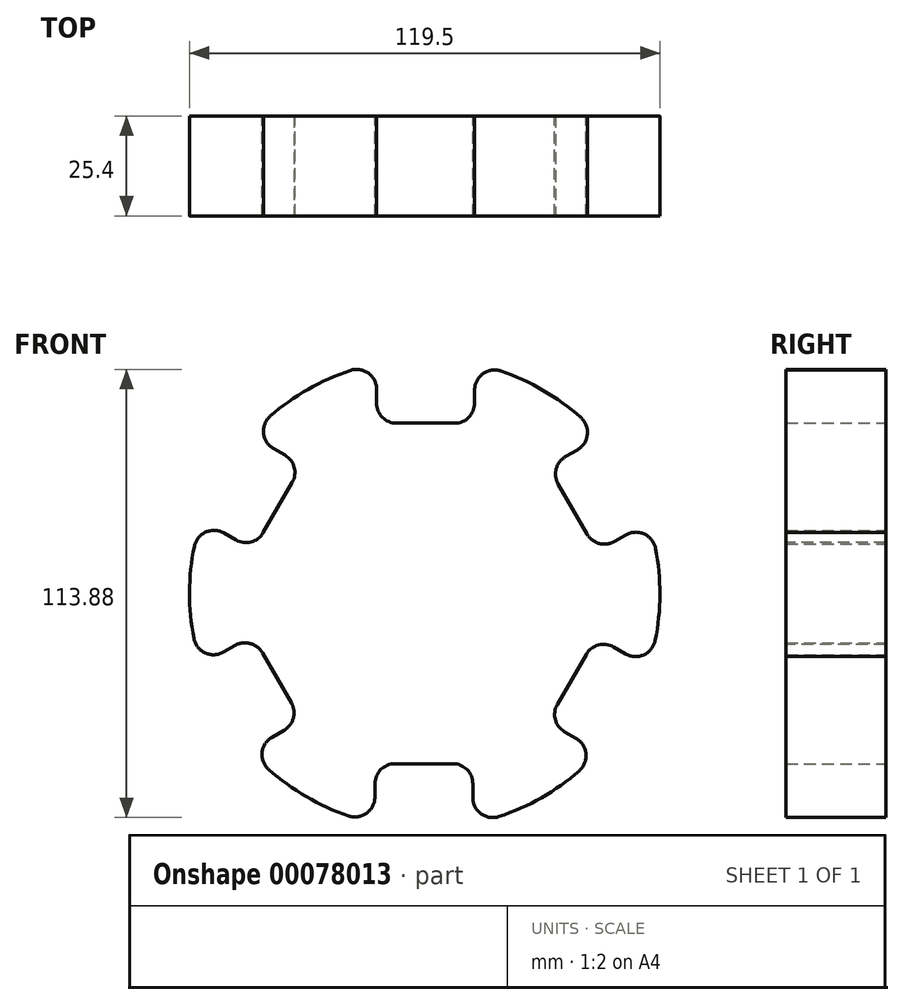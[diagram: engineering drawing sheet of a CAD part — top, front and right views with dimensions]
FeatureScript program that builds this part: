
annotation { "Feature Type Name" : "Feature", "Feature Type Description" : "" }
export const myFeature = defineFeature(function(context is Context, id is Id, definition is map)
    precondition{}
    {
        {
            var Q0;
            Q0=qCreatedBy(makeId("Front.planeOp"),FACE);
            var sketch = newSketch(context, id + "F0", { "sketchPlane" : qUnion([Q0])});
            skCircle(sketch, "E0", {"center": v(0, 0) * mm, "radius": 59.75 * mm});
            skSolve(sketch);
        }
        {
            var Q0;
            Q0=makeQuery(id+"F0.imprint","IMPRINT",FACE,{"disambiguationData":[TD([[makeQuery(id+"F0.imprint","IMPRINT",EDGE,{"derivedFrom":sQuery(id+"F0.wireOp",EDGE,"E0")}),1.0]])]});
            extrude(context, id + "F1", {"entities" : qUnion([Q0]), "depth" : 25.4 * mm});
        }
        {
            var Q0;
            Q0=qCreatedBy(makeId("Top.planeOp"),FACE);
            var sketch = newSketch(context, id + "F5", { "sketchPlane" : qUnion([Q0])});
            skLineSegment(sketch, "E1", {"start": v(0, 57.44) * mm, "end": v(0, -61.35) * mm, "construction": true});
            skSolve(sketch);
        }
        {
            var Q0;
            Q0=qCreatedBy(makeId("Front.planeOp"),FACE);
            var sketch = newSketch(context, id + "F2", { "sketchPlane" : qUnion([Q0])});
            skLineSegment(sketch, "E2.bottom", {"start": v(-12.22, 105.83) * mm, "end": v(12.67, 105.83) * mm});
            skLineSegment(sketch, "E2.top", {"start": v(-12.22, 43.26) * mm, "end": v(12.67, 43.26) * mm});
            skLineSegment(sketch, "E2.left", {"start": v(-12.22, 105.83) * mm, "end": v(-12.22, 43.26) * mm});
            skLineSegment(sketch, "E2.right", {"start": v(12.67, 105.83) * mm, "end": v(12.67, 43.26) * mm});
            skSolve(sketch);
        }
        {
            var Q0;
            Q0=makeQuery(id+"F2.imprint","IMPRINT",FACE,{"disambiguationData":[TD([[makeQuery(id+"F2.imprint","IMPRINT",EDGE,{"derivedFrom":sQuery(id+"F2.wireOp",EDGE,"E2.bottom")}),-1.0]])]});
            extrude(context, id + "F6", {"entities" : qUnion([Q0]), "operationType" : NewBodyOperationType.REMOVE, "depth" : 25.4 * mm});
        }
        {
            var Q0;
            Q0=makeQuery(id+"F6.boolean.opBoolean","INTERSECT",EDGE,{"derivedFrom":[makeQuery(id+"F1.opExtrude","SWEPT_FACE",FACE,{"disambiguationData":[OSD([sQuery(id+"F0.wireOp",EDGE,"E0")])]}),makeQuery(id+"F6.opExtrude","SWEPT_FACE",FACE,{"disambiguationData":[OSD([sQuery(id+"F2.wireOp",EDGE,"E2.left")])]})]});
            fillet(context, id + "F7", {"entities" : qUnion([Q0]), "radius" : 5.08 * mm, "tangentPropagation" : true, "allowEdgeOverflow" : false});
        }
        {
            var Q0;
            Q0=makeQuery(id+"F6.boolean.opBoolean","INTERSECT",EDGE,{"derivedFrom":[makeQuery(id+"F1.opExtrude","SWEPT_FACE",FACE,{"disambiguationData":[OSD([sQuery(id+"F0.wireOp",EDGE,"E0")])]}),makeQuery(id+"F6.opExtrude","SWEPT_FACE",FACE,{"disambiguationData":[OSD([sQuery(id+"F2.wireOp",EDGE,"E2.right")])]})]});
            var Q1;
            Q1=makeQuery(id+"F6.boolean.opBoolean","COPY",EDGE,{"derivedFrom":makeQuery(id+"F6.opExtrude","SWEPT_EDGE",EDGE,{"disambiguationData":[OSD([sQuery(id+"F2.wireOp",EDGE,"E2.top"),sQuery(id+"F2.wireOp",EDGE,"E2.right")])]})});
            var Q2;
            Q2=makeQuery(id+"F6.boolean.opBoolean","COPY",EDGE,{"derivedFrom":makeQuery(id+"F6.opExtrude","SWEPT_EDGE",EDGE,{"disambiguationData":[OSD([sQuery(id+"F2.wireOp",EDGE,"E2.top"),sQuery(id+"F2.wireOp",EDGE,"E2.left")])]})});
            fillet(context, id + "F3", {"entities" : qUnion([Q0, Q1, Q2]), "radius" : 5.08 * mm, "tangentPropagation" : true, "allowEdgeOverflow" : false});
        }
        {
            var Q0;
            Q0=makeQuery(id+"F1.opExtrude","SWEPT_BODY",BODY,{"disambiguationData":[OSD([sQuery(id+"F0.wireOp",EDGE,"E0")])]});
            var Q1;
            Q1=makeQuery(id+"F7.opFillet","BLEND_FACE",FACE,{"disambiguationData":[OSD([sQuery(id+"F0.wireOp",EDGE,"E0"),sQuery(id+"F2.wireOp",EDGE,"E2.left")])]});
            var Q2;
            Q2=makeQuery(id+"F3.opFillet","BLEND_FACE",FACE,{"disambiguationData":[OSD([sQuery(id+"F2.wireOp",EDGE,"E2.top"),sQuery(id+"F2.wireOp",EDGE,"E2.left")])]});
            var Q3;
            Q3=makeQuery(id+"F6.boolean.opBoolean","COPY",FACE,{"derivedFrom":makeQuery(id+"F6.opExtrude","SWEPT_FACE",FACE,{"disambiguationData":[OSD([sQuery(id+"F2.wireOp",EDGE,"E2.left")])]})});
            var Q4;
            Q4=makeQuery(id+"F6.boolean.opBoolean","COPY",FACE,{"derivedFrom":makeQuery(id+"F6.opExtrude","SWEPT_FACE",FACE,{"disambiguationData":[OSD([sQuery(id+"F2.wireOp",EDGE,"E2.top")])]})});
            var Q5;
            Q5=makeQuery(id+"F3.opFillet","BLEND_FACE",FACE,{"disambiguationData":[OSD([sQuery(id+"F2.wireOp",EDGE,"E2.top"),sQuery(id+"F2.wireOp",EDGE,"E2.right")])]});
            var Q6;
            Q6=makeQuery(id+"F6.boolean.opBoolean","COPY",FACE,{"derivedFrom":makeQuery(id+"F6.opExtrude","SWEPT_FACE",FACE,{"disambiguationData":[OSD([sQuery(id+"F2.wireOp",EDGE,"E2.right")])]})});
            var Q7;
            Q7=makeQuery(id+"F3.opFillet","BLEND_FACE",FACE,{"disambiguationData":[OSD([sQuery(id+"F0.wireOp",EDGE,"E0"),sQuery(id+"F2.wireOp",EDGE,"E2.right")])]});
            var Q8;
            Q8=sQuery(id+"F5.wireOp",EDGE,"E1");
            circularPattern(context, id + "F4", {"faces" : qUnion([Q1, Q2, Q3, Q4, Q5, Q6, Q7]), "axis" : qUnion([Q8]), "angle" : 30 * degree, "instanceCount" : 12, "patternType" : PatternType.FACE});
        }
    });
